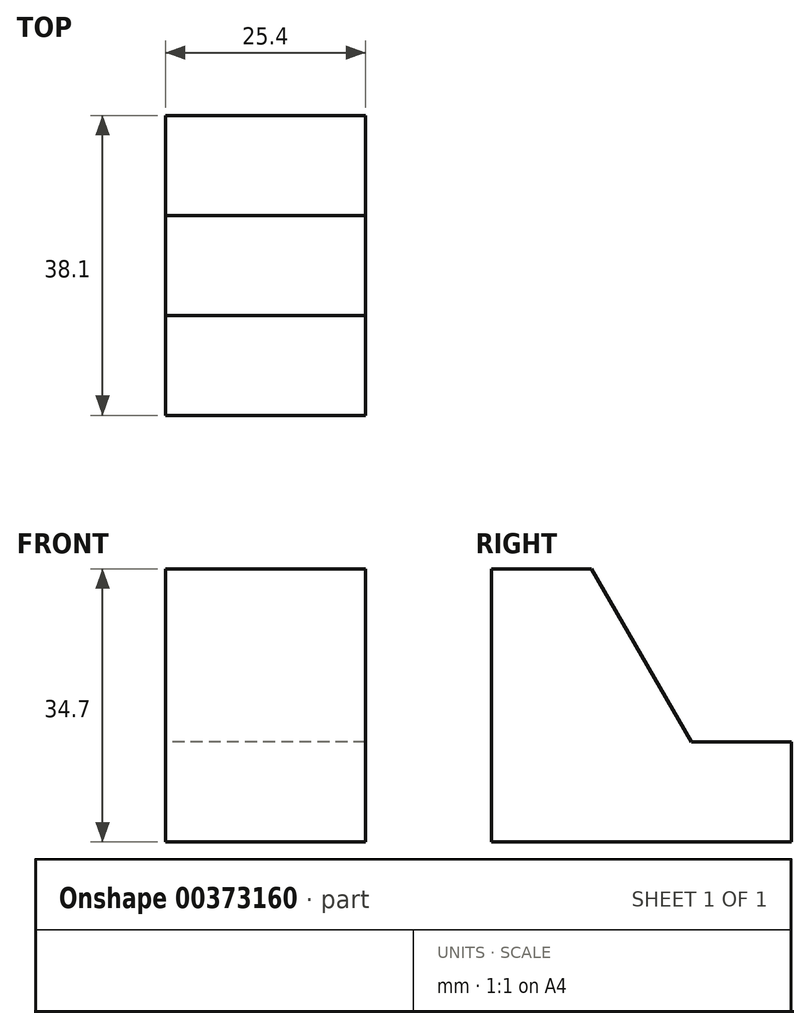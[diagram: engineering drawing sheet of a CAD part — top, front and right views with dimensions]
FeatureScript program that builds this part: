
annotation { "Feature Type Name" : "Feature", "Feature Type Description" : "" }
export const myFeature = defineFeature(function(context is Context, id is Id, definition is map)
    precondition{}
    {
        {
            var Q0;
            Q0=qCreatedBy(makeId("Right.planeOp"),FACE);
            var sketch = newSketch(context, id + "F0", { "sketchPlane" : qUnion([Q0])});
            skLineSegment(sketch, "E0", {"start": v(0, 0) * mm, "end": v(38.1, 0) * mm});
            skLineSegment(sketch, "E1", {"start": v(38.1, 0) * mm, "end": v(38.1, 12.7) * mm});
            skLineSegment(sketch, "E2", {"start": v(38.1, 12.7) * mm, "end": v(25.4, 12.7) * mm});
            skLineSegment(sketch, "E3", {"start": v(25.4, 12.7) * mm, "end": v(12.7, 34.7) * mm});
            skLineSegment(sketch, "E4", {"start": v(12.7, 34.7) * mm, "end": v(0, 34.7) * mm});
            skLineSegment(sketch, "E5", {"start": v(0, 34.7) * mm, "end": v(0, 0) * mm});
            skSolve(sketch);
        }
        {
            var Q0;
            Q0=makeQuery(id+"F0.imprint","IMPRINT",FACE,{"disambiguationData":[TD([[makeQuery(id+"F0.imprint","IMPRINT",EDGE,{"derivedFrom":sQuery(id+"F0.wireOp",EDGE,"E0")}),1.0]])]});
            extrude(context, id + "F1", {"entities" : qUnion([Q0]), "depth" : 25.4 * mm});
        }
    });
